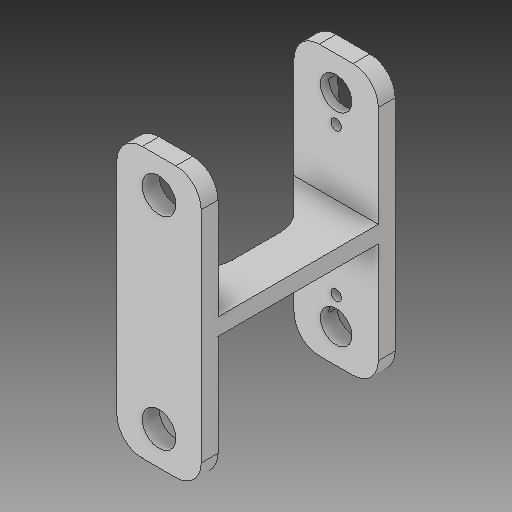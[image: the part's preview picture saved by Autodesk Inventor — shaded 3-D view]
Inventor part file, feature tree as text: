
AUTODESK INVENTOR PART (.ipt)
format: ipt  version: 2019 (Build 230136000, 136)  size: 289,792 bytes
history: native  units: mm
features: sketch x12, projected_geometry x11, extrude x6, hole x6, fillet x2, chamfer x1
ambient origin geometry x8: Origin, YZ Plane, XZ Plane, XY Plane, X Axis, Y Axis, Z Axis, Center Point
bodies: Solid1 (feature_tree)
feature tree (38):
  extrude  "Extrusion1"  Depth=20.0mm
  extrude  "Extrusion2"  Depth=4.0mm
  hole  "Hole1"  [1 undecoded]
  extrude  "Extrusion4"  Depth=8.0mm
  hole  "Hole4"  [1 undecoded]
  hole  "Hole5"  [1 undecoded]
  extrude  "Extrusion5"  Depth=2.0mm
  extrude  "Extrusion6"  Depth=8.0mm
  hole  "Hole6"  [1 undecoded]
  hole  "Hole7"  [1 undecoded]
  hole  "Hole8"  [1 undecoded]
  fillet  "Fillet4"  Radius=8.0mm
  extrude  "Extrusion8"  Depth=10.0mm
  chamfer  "Chamfer1"  Distance=7.5mm
  fillet  "Fillet6"  Radius=16.0mm
  sketch  "Sketch1"  dims[d0=46.0mm d1=20.0mm]
  sketch  "Sketch2"  dims[d2=4.0mm d3=0.0mm d4=4.0mm]
  projected_geometry  "Projected Loop1"
  sketch  "Sketch4"  dims[d5=4.0mm d6=30.0mm d7=0.0mm]
  projected_geometry  "Projected Loop2"
  sketch  "Sketch10"  dims[d8=10.0mm d9=8.0mm]
  projected_geometry  "Projected Loop7"
  sketch  "Sketch11"  dims[d10=8.0mm d11=6.0mm d12=4.0mm d13=2.0mm d14=90.0deg d15=8.0mm d16=0.0mm d47=16.5mm]
  projected_geometry  "Projected Loop8"
  sketch  "Sketch12"  dims[d48=7.5mm d49=5.0mm]
  projected_geometry  "Projected Loop9"
  sketch  "Sketch13"  dims[d50=10.0mm d51=2.0mm]
  projected_geometry  "Projected Loop10"
  sketch  "Sketch14"  dims[d52=2.0mm d53=8.0mm]
  projected_geometry  "Projected Loop11"
  sketch  "Sketch15"  dims[d54=8.0mm d55=2.0mm d56=0.0mm]
  projected_geometry  "Projected Loop12"
  sketch  "Sketch16"  dims[d57=7.5mm d58=6.0mm d59=4.0mm d60=2.0mm d61=90.0deg d62=8.0mm d63=0.0mm d64=6.5mm]
  projected_geometry  "Projected Loop13"
  projected_geometry  "Projected Loop14"
  sketch  "Sketch17"  dims[d65=10.0mm]
  sketch  "Sketch19"  dims[d66=2.5mm d67=6.0mm d68=4.0mm d69=2.0mm d70=90.0deg d71=8.0mm d72=0.0mm d75=30.0mm d76=0.0mm d77=8.0mm d78=10.0mm d79=7.5mm d80=16.0mm d81=5.0mm d82=10.0mm d85=2.0mm d86=8.0mm d87=2.0mm d88=8.0mm d89=2.0mm d90=0.0mm d91=7.5mm d92=6.0mm d93=4.0mm d94=2.0mm d95=90.0deg d96=8.0mm d97=0.0mm d98=10.0mm d99=6.5mm d100=2.5mm d101=6.0mm d102=4.0mm d103=2.0mm d104=90.0deg d105=8.0mm d106=0.0mm d107=8.0mm d108=10.0mm d109=8.0mm d110=6.0mm d111=4.0mm d112=2.0mm d113=90.0deg d114=4.0mm d115=0.0mm d116=6.0mm d124=2.0mm d125=0.0mm d126=10.0mm d127=2.0mm d128=45.0deg d129=8.0mm]
  projected_geometry  "Projected Loop16"
note: 6 required parameter values undecoded (feature->parameter linkage not recoverable at this tier; creation-order binding heuristic only, values carry confidence <= 0.55)
